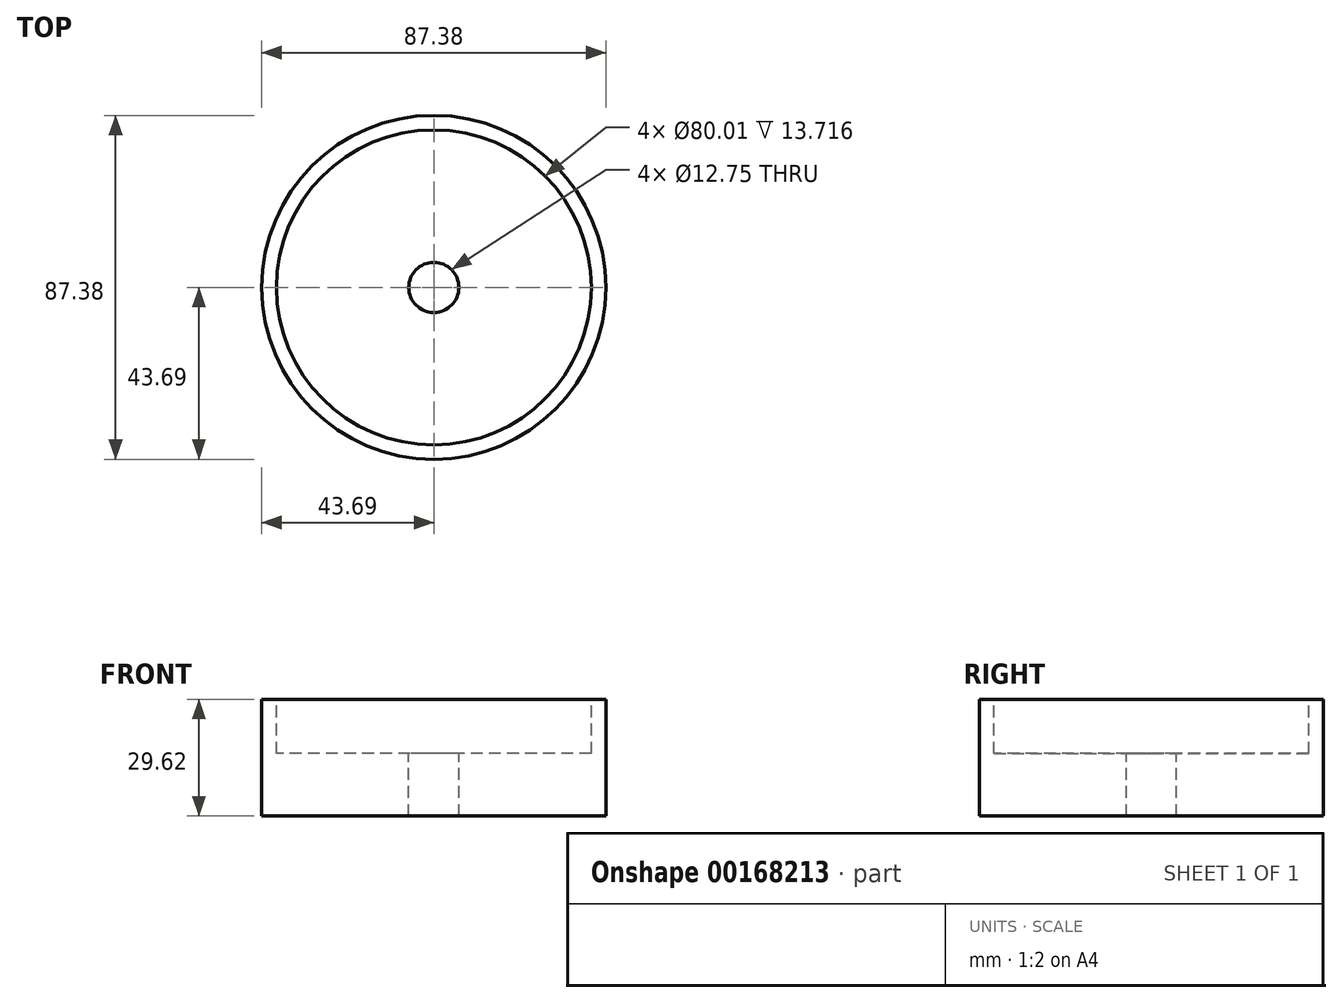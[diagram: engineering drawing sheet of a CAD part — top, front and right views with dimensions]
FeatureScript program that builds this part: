
annotation { "Feature Type Name" : "Feature", "Feature Type Description" : "" }
export const myFeature = defineFeature(function(context is Context, id is Id, definition is map)
    precondition{}
    {
        {
            var Q0;
            Q0=qCreatedBy(makeId("Top.planeOp"),FACE);
            var sketch = newSketch(context, id + "F0", { "sketchPlane" : qUnion([Q0])});
            skCircle(sketch, "E0", {"center": v(0, 0) * mm, "radius": 43.69 * mm});
            skSolve(sketch);
        }
        {
            var Q0;
            Q0=qSketchRegion(id+"F0",true);
            extrude(context, id + "F1", {"entities" : qUnion([Q0]), "depth" : 29.62 * mm});
        }
        {
            var Q0;
            Q0=makeQuery(id+"F1.opExtrude","CAP_FACE",FACE,{"disambiguationData":[OSD([sQuery(id+"F0.wireOp",EDGE,"E0")])],"isStart":false});
            var sketch = newSketch(context, id + "F2", { "sketchPlane" : qUnion([Q0])});
            skCircle(sketch, "E1", {"center": v(0, 0) * mm, "radius": 40 * mm});
            skSolve(sketch);
        }
        {
            var Q0;
            Q0 = qSketchRegion(id + "F2", true);
            extrude(context, id + "F3", {"entities" : qUnion([Q0]), "operationType" : NewBodyOperationType.REMOVE, "oppositeDirection" : true, "depth" : 13.72 * mm});
        }
        {
            var Q0;
            Q0=makeQuery(id+"F3.boolean.opBoolean","COPY",FACE,{"derivedFrom":makeQuery(id+"F3.opExtrude","CAP_FACE",FACE,{"disambiguationData":[OSD([sQuery(id+"F2.wireOp",EDGE,"E1")])],"isStart":false})});
            var sketch = newSketch(context, id + "F4", { "sketchPlane" : qUnion([Q0])});
            skCircle(sketch, "E2", {"center": v(0, 0) * mm, "radius": 6.38 * mm});
            skSolve(sketch);
        }
        {
            var Q0;
            Q0 = qSketchRegion(id + "F4", true);
            var Q1;
            Q1=sQuery(id+"F4.wireOp",EDGE,"E2");
            extrude(context, id + "F5", {"entities" : qUnion([Q0]), "operationType" : NewBodyOperationType.REMOVE, "surfaceEntities" : qUnion([Q1]), "endBound" : BoundingType.THROUGH_ALL, "oppositeDirection" : true, "depth" : 25.4 * mm});
        }
    });
